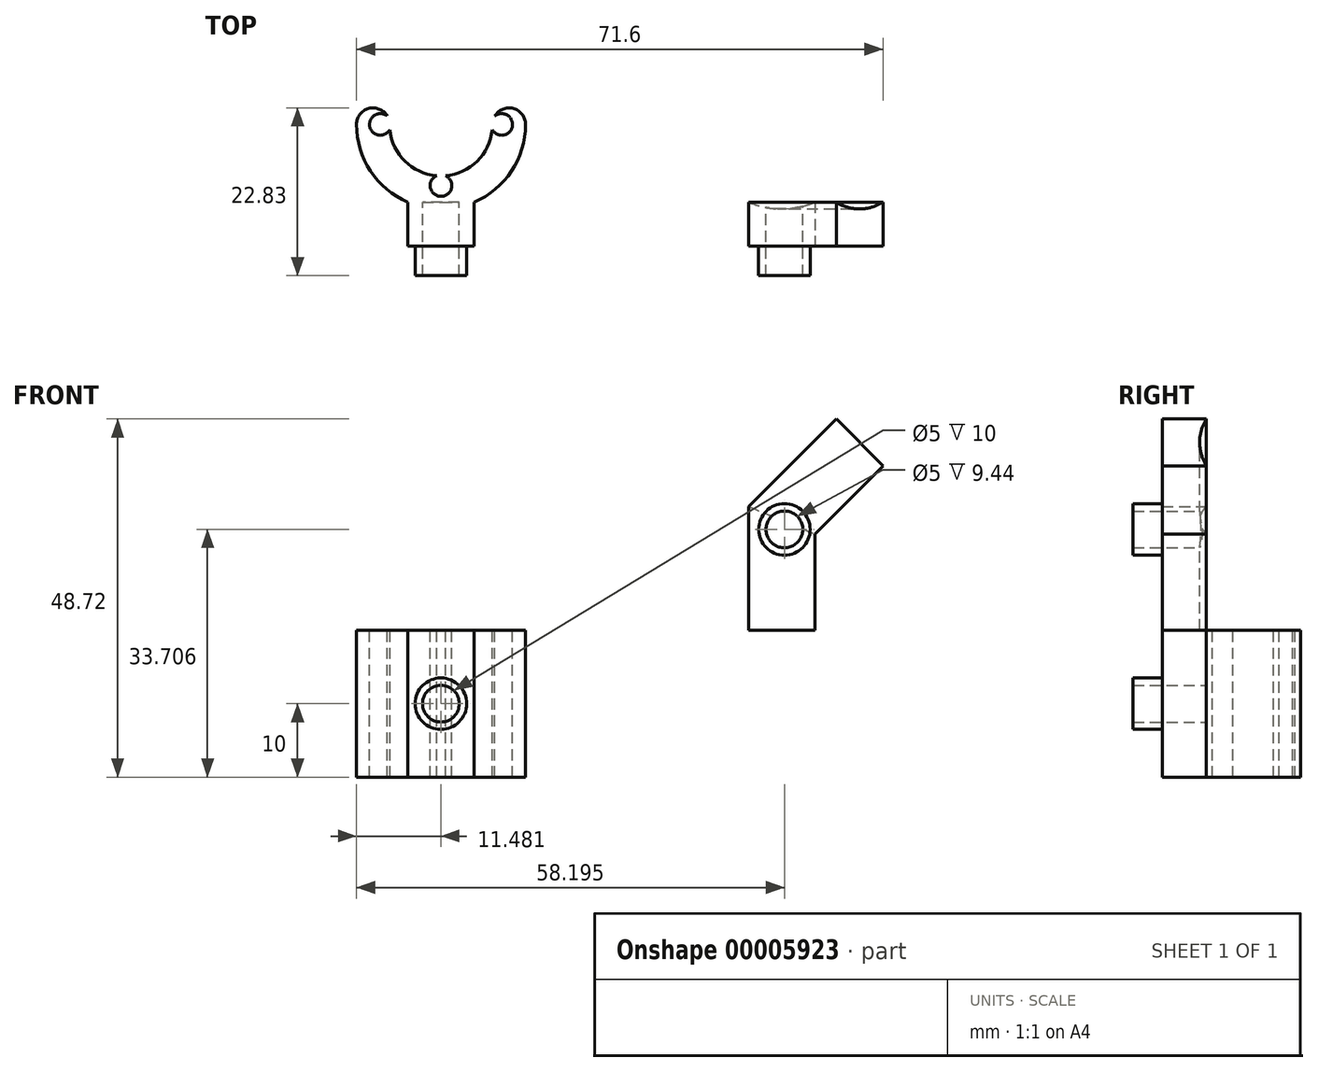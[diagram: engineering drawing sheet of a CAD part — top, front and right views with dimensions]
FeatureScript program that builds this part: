
annotation { "Feature Type Name" : "Feature", "Feature Type Description" : "" }
export const myFeature = defineFeature(function(context is Context, id is Id, definition is map)
    precondition{}
    {
        {
            var Q0;
            Q0=qCreatedBy(makeId("Top.planeOp"),FACE);
            var sketch = newSketch(context, id + "F0", { "sketchPlane" : qUnion([Q0])});
            skArc(sketch, "E0", {"start": v(-14, 0) * mm, "mid": v(-7, -7) * mm, "end": v(0, 0) * mm});
            skArc(sketch, "E1.0", {"start": v(-18.5, 0) * mm, "mid": v(-7, -11.5) * mm, "end": v(4.5, 0) * mm});
            skArc(sketch, "E2", {"start": v(-14, 0) * mm, "mid": v(-16.25, 2.25) * mm, "end": v(-18.5, 0) * mm});
            skArc(sketch, "E3", {"start": v(4.5, 0) * mm, "mid": v(2.25, 2.25) * mm, "end": v(0, 0) * mm});
            skCircle(sketch, "E4", {"center": v(-15.25, 0) * mm, "radius": 1.48 * mm});
            skLineSegment(sketch, "E5", {"start": v(-7, 4.35) * mm, "end": v(-7, -12.6) * mm, "construction": true});
            skCircle(sketch, "E6.0.MirrorC", {"center": v(1.25, 0) * mm, "radius": 1.48 * mm});
            skCircle(sketch, "E7", {"center": v(-7, -8.32) * mm, "radius": 1.48 * mm});
            skArc(sketch, "E8", {"start": v(-15.25, 0) * mm, "mid": v(-7, -8.32) * mm, "end": v(1.25, 0) * mm, "construction": true});
            skLineSegment(sketch, "E9", {"start": v(-11.52, -10.58) * mm, "end": v(-11.52, -16.58) * mm});
            skLineSegment(sketch, "E10", {"start": v(-11.52, -16.58) * mm, "end": v(-2.52, -16.58) * mm});
            skLineSegment(sketch, "E11", {"start": v(-2.52, -16.58) * mm, "end": v(-2.52, -10.6) * mm});
            skLineSegment(sketch, "E12", {"start": v(-7, -12.6) * mm, "end": v(-7, -16.58) * mm, "construction": true});
            skLineSegment(sketch, "E13", {"start": v(16.16, 11.08) * mm, "end": v(16.16, -23.86) * mm, "construction": true});
            skArc(sketch, "E14.0.MirrorCS", {"start": v(46.32, 0) * mm, "mid": v(48.57, 2.25) * mm, "end": v(50.82, 0) * mm});
            skLineSegment(sketch, "E14.1.MirrorCS", {"start": v(43.84, -10.58) * mm, "end": v(43.84, -16.58) * mm});
            skLineSegment(sketch, "E14.2.MirrorCS", {"start": v(39.32, -12.6) * mm, "end": v(39.32, -16.58) * mm, "construction": true});
            skLineSegment(sketch, "E14.3.MirrorCS", {"start": v(43.84, -16.58) * mm, "end": v(34.84, -16.58) * mm});
            skArc(sketch, "E14.4.MirrorCS", {"start": v(47.57, 0) * mm, "mid": v(39.32, -8.32) * mm, "end": v(31.07, 0) * mm, "construction": true});
            skCircle(sketch, "E14.5.MirrorC", {"center": v(39.32, -8.32) * mm, "radius": 1.48 * mm});
            skCircle(sketch, "E14.6.MirrorC", {"center": v(31.07, 0) * mm, "radius": 1.48 * mm});
            skLineSegment(sketch, "E14.7.MirrorCS", {"start": v(34.84, -16.58) * mm, "end": v(34.84, -10.6) * mm});
            skArc(sketch, "E14.8.MirrorCS", {"start": v(27.82, 0) * mm, "mid": v(30.07, 2.25) * mm, "end": v(32.32, 0) * mm});
            skCircle(sketch, "E14.9.MirrorC", {"center": v(47.57, 0) * mm, "radius": 1.48 * mm});
            skArc(sketch, "E14.10.MirrorCS", {"start": v(46.32, 0) * mm, "mid": v(39.32, -7) * mm, "end": v(32.32, 0) * mm});
            skArc(sketch, "E14.11.MirrorCS", {"start": v(50.82, 0) * mm, "mid": v(39.32, -11.5) * mm, "end": v(27.82, 0) * mm});
            skLineSegment(sketch, "E14.12.MirrorCS", {"start": v(39.32, 4.35) * mm, "end": v(39.32, -12.6) * mm, "construction": true});
            skSolve(sketch);
        }
        {
            var Q0;
            {var subQ1=sQuery(id+"F0.wireOp",EDGE,"E0");var subQ8=sQuery(id+"F0.wireOp",EDGE,"E4");var subQ11=makeQuery(id+"F0.imprint","INTERSECT",VERTEX,{"derivedFrom":[subQ1,subQ8]});Q0=makeQuery(id+"F0.imprint","IMPRINT",FACE,{"disambiguationData":[TD([[makeQuery(id+"F0.imprint","IMPRINT",EDGE,{"disambiguationData":[TD([[subQ11,-1.0]])],"derivedFrom":subQ1}),-1.0]])]});}
            var Q1;
            {var subQ1=sQuery(id+"F0.wireOp",EDGE,"E9");Q1=makeQuery(id+"F0.imprint","IMPRINT",FACE,{"disambiguationData":[TD([[makeQuery(id+"F0.imprint","IMPRINT",EDGE,{"derivedFrom":subQ1}),1.0]])]});}
            extrude(context, id + "F1", {"entities" : qUnion([Q0, Q1]), "oppositeDirection" : true, "depth" : 20 * mm});
        }
        {
            var Q0;
            Q0=makeQuery(id+"F1.opExtrude","SWEPT_FACE",FACE,{"disambiguationData":[OSD([sQuery(id+"F0.wireOp",EDGE,"E10")])]});
            var sketch = newSketch(context, id + "F2", { "sketchPlane" : qUnion([Q0])});
            skLineSegment(sketch, "E15", {"start": v(-11.52, -10) * mm, "end": v(-2.52, -10) * mm, "construction": true});
            skLineSegment(sketch, "E16", {"start": v(-7.02, 0) * mm, "end": v(-7.02, -20) * mm, "construction": true});
            skCircle(sketch, "E17", {"center": v(-7.02, -10) * mm, "radius": 2.5 * mm});
            skCircle(sketch, "E18.0", {"center": v(-7.02, -10) * mm, "radius": 3.5 * mm});
            skSolve(sketch);
        }
        {
            var Q0;
            Q0=makeQuery(id+"F2.imprint","IMPRINT",FACE,{"disambiguationData":[TD([[makeQuery(id+"F2.imprint","IMPRINT",EDGE,{"derivedFrom":sQuery(id+"F2.wireOp",EDGE,"E17")}),-1.0]])]});
            extrude(context, id + "F3", {"entities" : qUnion([Q0]), "operationType" : NewBodyOperationType.ADD, "depth" : 4 * mm});
        }
        {
            var Q0;
            Q0=makeQuery(id+"F3.boolean.opBoolean","SPLIT",FACE,{"disambiguationData":[TD([makeQuery(id+"F3.opExtrude","SWEPT_FACE",FACE,{"disambiguationData":[OSD([sQuery(id+"F2.wireOp",EDGE,"E17")])]})])],"derivedFrom":makeQuery(id+"F1.opExtrude","SWEPT_FACE",FACE,{"disambiguationData":[OSD([sQuery(id+"F0.wireOp",EDGE,"E10")])]})});
            extrude(context, id + "F4", {"entities" : qUnion([Q0]), "operationType" : NewBodyOperationType.REMOVE, "oppositeDirection" : true, "depth" : 6 * mm});
        }
        {
            var Q0;
            Q0=qCreatedBy(makeId("Front.planeOp"),FACE);
            var sketch = newSketch(context, id + "F5", { "sketchPlane" : qUnion([Q0])});
            skLineSegment(sketch, "E19", {"start": v(39.25, 0) * mm, "end": v(39.25, 15) * mm});
            skLineSegment(sketch, "E20", {"start": v(39.25, 15) * mm, "end": v(49.85, 25.6) * mm});
            skSolve(sketch);
        }
        {
            var Q0;
            {var subQ2=sQuery(id+"F0.wireOp",EDGE,"E14.1.MirrorCS");Q0=makeQuery(id+"F0.imprint","IMPRINT",FACE,{"disambiguationData":[TD([[makeQuery(id+"F0.imprint","IMPRINT",EDGE,{"derivedFrom":subQ2}),-1.0]])]});}
            var Q1;
            {var subQ0=sQuery(id+"F0.wireOp",EDGE,"E14.11.MirrorCS");var subQ13=sQuery(id+"F0.wireOp",EDGE,"E14.0.MirrorCS");var subQ14=makeQuery(id+"F0.imprint","INTERSECT",VERTEX,{"derivedFrom":[subQ13,subQ0]});Q1=makeQuery(id+"F0.imprint","IMPRINT",FACE,{"disambiguationData":[TD([[makeQuery(id+"F0.imprint","IMPRINT",EDGE,{"disambiguationData":[TD([[subQ14,1.0]])],"derivedFrom":subQ13}),-1.0]])]});}
            var Q2;
            Q2=sQuery(id+"F5.wireOp",EDGE,"E19");
            var Q3;
            Q3=sQuery(id+"F5.wireOp",EDGE,"E20");
            sweep(context, id + "F6", {"profiles" : qUnion([Q0, Q1]), "path" : qUnion([Q2, Q3])});
        }
        {
            var Q0;
            Q0=makeQuery(id+"F6.opSweep","SWEPT_FACE",FACE,{"disambiguationData":[OSD([sQuery(id+"F0.wireOp",EDGE,"E14.3.MirrorCS"),sQuery(id+"F5.wireOp",EDGE,"E19")])]});
            var sketch = newSketch(context, id + "F7", { "sketchPlane" : qUnion([Q0])});
            skCircle(sketch, "E21", {"center": v(39.7, 13.7) * mm, "radius": 2.5 * mm});
            skCircle(sketch, "E22.0", {"center": v(39.7, 13.7) * mm, "radius": 3.5 * mm});
            skSolve(sketch);
        }
        {
            var Q0;
            Q0=makeQuery(id+"F7.imprint","IMPRINT",FACE,{"disambiguationData":[TD([[makeQuery(id+"F7.imprint","IMPRINT",EDGE,{"derivedFrom":sQuery(id+"F7.wireOp",EDGE,"E21")}),-1.0]])]});
            extrude(context, id + "F8", {"entities" : qUnion([Q0]), "operationType" : NewBodyOperationType.ADD, "depth" : 4 * mm});
        }
        {
            var Q0;
            Q0=makeQuery(id+"F8.boolean.opBoolean","SPLIT",FACE,{"disambiguationData":[TD([makeQuery(id+"F8.opExtrude","SWEPT_FACE",FACE,{"disambiguationData":[OSD([sQuery(id+"F7.wireOp",EDGE,"E21")])]})])],"derivedFrom":makeQuery(id+"F6.opSweep","SWEPT_FACE",FACE,{"disambiguationData":[OSD([sQuery(id+"F0.wireOp",EDGE,"E14.3.MirrorCS"),sQuery(id+"F5.wireOp",EDGE,"E19")])]})});
            extrude(context, id + "F9", {"entities" : qUnion([Q0]), "operationType" : NewBodyOperationType.REMOVE, "oppositeDirection" : true, "depth" : 6 * mm});
        }
    });
